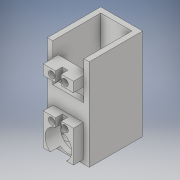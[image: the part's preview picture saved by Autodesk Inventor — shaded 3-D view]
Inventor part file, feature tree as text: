
AUTODESK INVENTOR PART (.ipt)
format: ipt  version: 2018 (Build 220112000, 112)  size: 302,080 bytes
history: native  units: in
note: dims shown in document units (in); Inventor stores cm internally (conversion verified against a paired STEP export)
features: sketch x15, extrude x11, hole x3, shell x1
ambient origin geometry x8: Origin, YZ Plane, XZ Plane, XY Plane, X Axis, Y Axis, Z Axis, Center Point
bodies: Solid1 (feature_tree)
feature tree (30):
  extrude  "Extrusion1"  Depth=1.0in
  shell  "Shell1"  Thickness=1.0in
  hole  "Hole1"  [1 undecoded]
  hole  "Hole2"  [1 undecoded]
  sketch  "Sketch4"  dims[d8=0.425in d9=0.25in]
  sketch  "Sketch5"  dims[d10=0.2in d11=0.125in]
  extrude  "Extrusion2"  Depth=0.25in
  extrude  "Extrusion3"  Depth=0.125in
  extrude  "Extrusion5"  Depth=0.125in
  extrude  "Extrusion6"  Depth=0.268in
  hole  "Hole4"  [1 undecoded]
  extrude  "Extrusion7"  Depth=0.5in
  extrude  "Extrusion8"  Depth=0.1in
  extrude  "Extrusion9"  Depth=0.565in
  extrude  "Extrusion10"  Depth=0.2675in
  extrude  "Extrusion11"  Depth=0.5in
  extrude  "Extrusion12"  Depth=1.0in
  sketch  "Sketch1"  dims[d0=0.785in d1=1.0in d2=1.0in d3=0.0in]
  sketch  "Sketch2"  dims[d4=0.1in d5=0.3925in]
  sketch  "Sketch3"  dims[d6=0.375in d7=0.6in]
  sketch  "Sketch6"  dims[d12=0.312in d13=0.125in]
  sketch  "Sketch9"  dims[d15=0.2675in d16=0.268in]
  sketch  "Sketch10"  dims[d17=0.125in d18=0.75in d19=0.375in d20=0.25in d21=0.5635in d22=0.3in d23=0.8108in d24=0.275in]
  sketch  "Sketch11"  dims[d25=0.5in d26=0.275in]
  sketch  "Sketch12"  dims[d27=0.3925in]
  sketch  "Sketch13"  dims[d28=0.5in d29=0.75in d30=0.375in d31=0.25in d32=0.5635in d33=0.1in d34=0.8108in d35=0.375in]
  sketch  "Sketch14"  dims[d36=0.565in d38=0.393in]
  sketch  "Sketch15"  dims[d39=0.268in d40=0.2675in]
  sketch  "Sketch16"  dims[d41=0.5in d42=0.3925in]
  sketch  "Sketch17"  dims[d43=0.2in d44=0.313in d45=0.313in d46=0.1875in d47=0.0in d48=0.105in d49=0.23in d50=0.125in d51=0.0in d56=0.2495in d66=0.075in d71=1.5in d75=0.1105in d76=0.1095in d77=0.2in d78=0.0in d79=0.2in d80=0.0in d81=0.2675in d83=0.125in d84=0.75in d85=0.375in d86=0.25in d87=0.5635in d88=0.6in d89=0.8108in d91=0.5in d92=0.5in d93=0.25in d94=0.2in d95=0.4in d96=0.4in d97=0.4in d98=0.2in d99=0.0725in d100=0.073in d101=0.1875in d102=0.1875in d103=0.7143in d104=0.0in d105=0.1in d106=0.1in d107=1.0in d108=0.7143in d109=0.0in d110=0.1in d111=0.1875in d112=0.0in d115=0.1in d116=0.0in d119=0.0in d120=0.125in d121=0.0in d122=0.125in d123=0.125in d124=0.268in d125=0.268in d126=0.375in d127=0.375in d128=0.5in d129=0.0in d130=0.105in d133=0.23in d134=0.0in d135=0.0in d136=0.1in d137=0.0in d82=1.0in]
note: 3 required parameter values undecoded (feature->parameter linkage not recoverable at this tier; creation-order binding heuristic only, values carry confidence <= 0.55)
